# Revit family: spectral_perga_perga-qe_455_2600-840_ws_a65f
name_source: partatom
category: Lighting Fixtures
revit_build: Autodesk Revit 2016 (Build: 20150220_1215(x64)
units: mm (PartAtom-declared; Revit-internal decimal feet)

## family parameters
Cut with Voids When Loaded = No
Host = Face
Light Source = No
Part Type = Normal
Room Calculation Point = No
Round Connector Dimension = Use Diameter
Shared = No

## types (1)
- SPECTRAL PERGA (1 x )
    Apparent Load = 0 VA
    Approval mark = CE
    CIE Flux Codes = 46 78 95 88 63
    Control Gear = Electronic transformer
    Default Elevation = 1800 mm
    Description = SPP0000016
PERGAMENT recessed luminaire

Design:
Square luminaire element in acrylic glass with transparent superpolished exterior. Underneath painted matt, scratchproof and insensitive to fingerprints. Luminaire element integrated in an outer steel frame designed for snap fixture into the recessed ceiling housing. Steel housing for inserting into the ceiling cut-out and fixture using steel spring clips. Recessed ceiling housing accommodates the electrical components and electronic ballast. All metal parts powder coated. Luminaire with heat-resistant wiring. Protection rating IP20, Safety class I.

Colour:
Gear tray – similar to RAL 9016 white silk matt
Frame – white, silver, black
    Height = 0 mm  [stored 0 ft]
    Lamp = 1 x
    Lamp count = 1
    Length = 455 mm
    Luminous efficacy = 0 lm/W
    Manufacturer = Ridi
    ModVariant = No
    Model = PERGA-QE 455/2600-840 WS
    Mounting Place = Ceiling
    Mounting Type = Recessed
    Number of Poles = 1
    OnlyDefault = Yes
    Power Factor = 1
    Product Name = SPECTRAL PERGA
    Product group = Recessed luminaire
    ProductGroupID = 4
    Protection Class = Protection class
    Protection Degree = IP 20
    RlxData = <blob elided: 24021 chars, md5=b70c525b>
    Socket = socket
    Standby Power = 0 W
    System Light Flux = 0 lm
    System Power = 0 W
    Type Image = pergeinbquaddet08.jpg
    URL = http://reluxnet.relux.com
    VarID = 1
    Voltage = 0 V
    Weight = 0.00 kg
    Width = 455 mm

note: [stored X ft] marks values corroborated as IEEE doubles in the binary element streams (Revit-internal decimal feet)

## geometry (parser evidence)
native form markers: Blend x4, Sweep x15
no freeform markers — native parametric forms only
